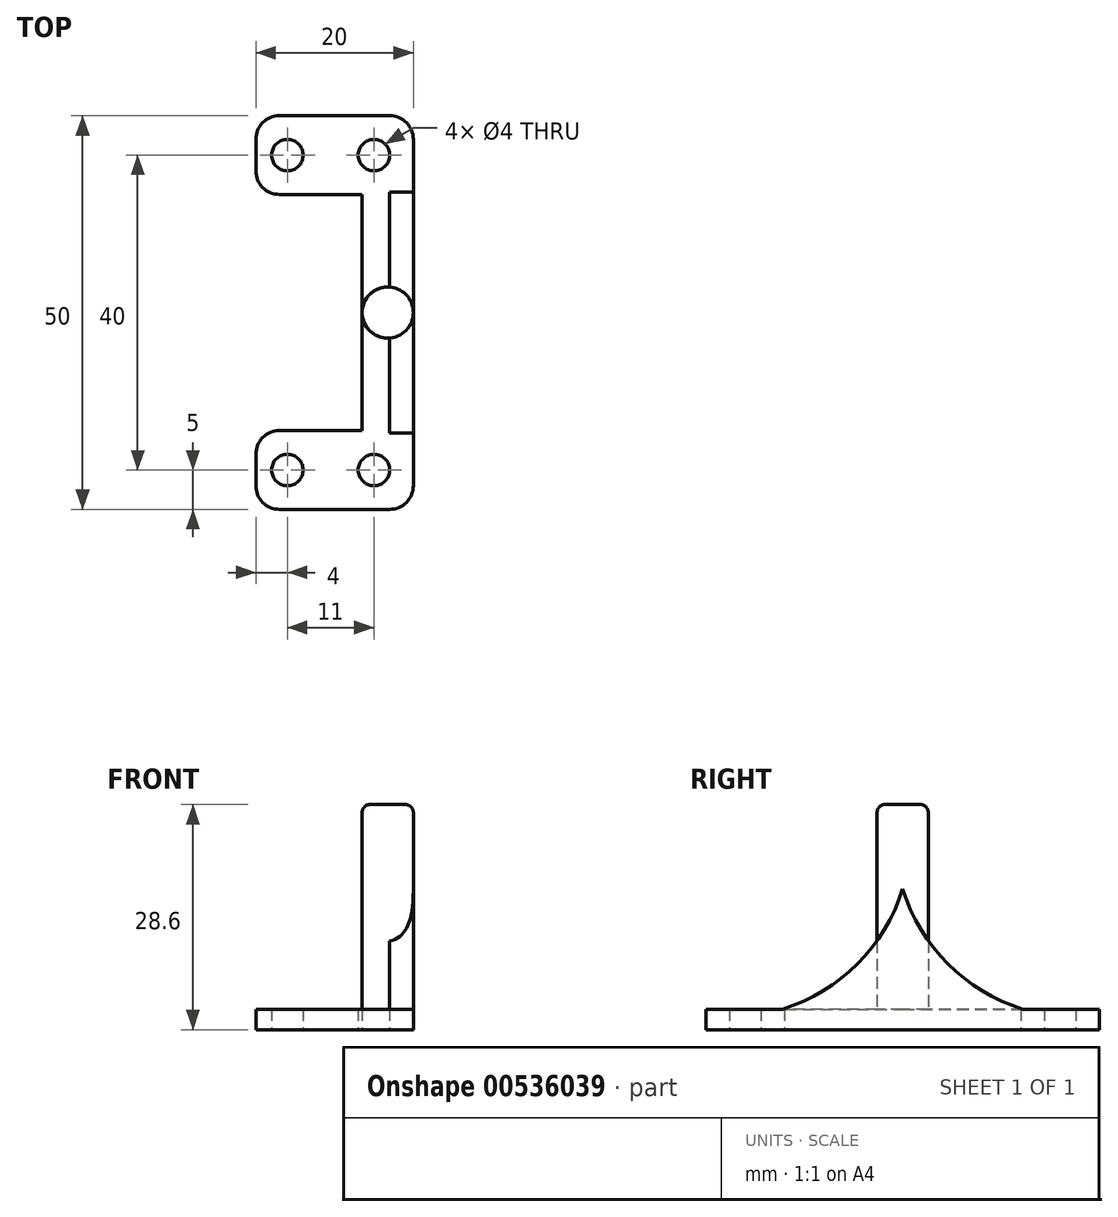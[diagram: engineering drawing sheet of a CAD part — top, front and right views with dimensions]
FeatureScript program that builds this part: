
annotation { "Feature Type Name" : "Feature", "Feature Type Description" : "" }
export const myFeature = defineFeature(function(context is Context, id is Id, definition is map)
    precondition{}
    {
        {
            var Q0;
            Q0=qCreatedBy(makeId("Top.planeOp"),FACE);
            var sketch = newSketch(context, id + "F0", { "sketchPlane" : qUnion([Q0])});
            skLineSegment(sketch, "E0.bottom", {"start": v(-20, 50) * mm, "end": v(0, 50) * mm});
            skLineSegment(sketch, "E0.right", {"start": v(0, 50) * mm, "end": v(0, 0) * mm});
            skLineSegment(sketch, "E1", {"start": v(-20, 50) * mm, "end": v(-20, 40) * mm});
            skLineSegment(sketch, "E2", {"start": v(-20, 10) * mm, "end": v(-6.5, 10) * mm});
            skLineSegment(sketch, "E3", {"start": v(-20, 40) * mm, "end": v(-6.5, 40) * mm});
            skCircle(sketch, "E4", {"center": v(-16, 45) * mm, "radius": 2 * mm});
            skCircle(sketch, "E5", {"center": v(-5, 45) * mm, "radius": 2 * mm});
            skCircle(sketch, "E6", {"center": v(-16, 5) * mm, "radius": 2 * mm});
            skCircle(sketch, "E7", {"center": v(-5, 5) * mm, "radius": 2 * mm});
            skLineSegment(sketch, "E8", {"start": v(-20, 10) * mm, "end": v(-20, 0) * mm});
            skLineSegment(sketch, "E9", {"start": v(-20, 0) * mm, "end": v(0, 0) * mm});
            skLineSegment(sketch, "E10", {"start": v(-6.5, 10) * mm, "end": v(-6.5, 40) * mm});
            skSolve(sketch);
        }
        {
            var Q0;
            Q0=makeQuery(id+"F0.imprint","IMPRINT",FACE,{"disambiguationData":[TD([[makeQuery(id+"F0.imprint","IMPRINT",EDGE,{"derivedFrom":sQuery(id+"F0.wireOp",EDGE,"E0.bottom")}),-1.0]])]});
            extrude(context, id + "F1", {"entities" : qUnion([Q0]), "depth" : 2.6 * mm, "offsetDistance" : 25 * mm});
        }
        {
            var Q0;
            Q0=makeQuery(id+"F1.opExtrude","CAP_FACE",FACE,{"disambiguationData":[OSD([sQuery(id+"F0.wireOp",EDGE,"E0.bottom"),sQuery(id+"F0.wireOp",EDGE,"E0.right"),sQuery(id+"F0.wireOp",EDGE,"E1"),sQuery(id+"F0.wireOp",EDGE,"5VIroKza-7dJa-2zdZ-CHlb-RgMu5IRMn0VJ"),sQuery(id+"F0.wireOp",EDGE,"E2"),sQuery(id+"F0.wireOp",EDGE,"E3"),sQuery(id+"F0.wireOp",EDGE,"E4"),sQuery(id+"F0.wireOp",EDGE,"E5"),sQuery(id+"F0.wireOp",EDGE,"E6"),sQuery(id+"F0.wireOp",EDGE,"E7"),sQuery(id+"F0.wireOp",EDGE,"E8"),sQuery(id+"F0.wireOp",EDGE,"E9"),sQuery(id+"F0.wireOp",EDGE,"IBOXaNeZ-d4qg-PSxC-ytc1-1ycewHry0LgP"),sQuery(id+"F0.wireOp",EDGE,"04bec0b6-6763-46f3-8f07-8cebe3ee9a99.trimOffspring")])],"isStart":false});
            var sketch = newSketch(context, id + "F2", { "sketchPlane" : qUnion([Q0])});
            skCircle(sketch, "E11", {"center": v(-3.25, 25) * mm, "radius": 3.25 * mm});
            skSolve(sketch);
        }
        {
            var Q0;
            Q0 = qSketchRegion(id + "F2", true);
            extrude(context, id + "F3", {"entities" : qUnion([Q0]), "operationType" : NewBodyOperationType.ADD, "depth" : 26 * mm, "offsetDistance" : 25 * mm});
        }
        {
            var Q0;
            Q0=makeQuery(id+"F1.opExtrude","SWEPT_EDGE",EDGE,{"disambiguationData":[OSD([sQuery(id+"F0.wireOp",EDGE,"E0.bottom"),sQuery(id+"F0.wireOp",EDGE,"E1")])]});
            var Q1;
            Q1=makeQuery(id+"F1.opExtrude","SWEPT_EDGE",EDGE,{"disambiguationData":[OSD([sQuery(id+"F0.wireOp",EDGE,"E1"),sQuery(id+"F0.wireOp",EDGE,"E3")])]});
            var Q2;
            Q2=makeQuery(id+"F1.opExtrude","SWEPT_EDGE",EDGE,{"disambiguationData":[OSD([sQuery(id+"F0.wireOp",EDGE,"E2"),sQuery(id+"F0.wireOp",EDGE,"E8")])]});
            var Q3;
            Q3=makeQuery(id+"F1.opExtrude","SWEPT_EDGE",EDGE,{"disambiguationData":[OSD([sQuery(id+"F0.wireOp",EDGE,"E8"),sQuery(id+"F0.wireOp",EDGE,"E9")])]});
            var Q4;
            Q4=makeQuery(id+"F1.opExtrude","SWEPT_EDGE",EDGE,{"disambiguationData":[OSD([sQuery(id+"F0.wireOp",EDGE,"E0.bottom"),sQuery(id+"F0.wireOp",EDGE,"E0.right")])]});
            var Q5;
            Q5=makeQuery(id+"F1.opExtrude","SWEPT_EDGE",EDGE,{"disambiguationData":[OSD([sQuery(id+"F0.wireOp",EDGE,"E0.right"),sQuery(id+"F0.wireOp",EDGE,"E9")])]});
            fillet(context, id + "F4", {"entities" : qUnion([Q0, Q1, Q2, Q3, Q4, Q5]), "radius" : 3 * mm, "tangentPropagation" : true, "allowEdgeOverflow" : false});
        }
        {
            var Q0;
            Q0=makeQuery(id+"F1.opExtrude","SWEPT_FACE",FACE,{"disambiguationData":[OSD([sQuery(id+"F0.wireOp",EDGE,"E0.right")])]});
            var sketch = newSketch(context, id + "F5", { "sketchPlane" : qUnion([Q0])});
            skArc(sketch, "E12", {"start": v(9.7, 2.6) * mm, "mid": v(19.26, 8.34) * mm, "end": v(25, 17.9) * mm});
            skArc(sketch, "E13", {"start": v(25, 17.9) * mm, "mid": v(30.74, 8.34) * mm, "end": v(40.3, 2.6) * mm});
            skSolve(sketch);
        }
        {
            var Q0;
            {var subQ0=sQuery(id+"F5.wireOp",EDGE,"E12");Q0=makeQuery(id+"F5.imprint","IMPRINT",FACE,{"disambiguationData":[TD([[makeQuery(id+"F5.imprint","IMPRINT",EDGE,{"derivedFrom":subQ0}),-1.0]])]});}
            extrude(context, id + "F6", {"entities" : qUnion([Q0]), "operationType" : NewBodyOperationType.ADD, "oppositeDirection" : true, "depth" : 3 * mm, "offsetDistance" : 25 * mm});
        }
        {
            var Q0;
            Q0=makeQuery(id+"F3.opExtrude","CAP_EDGE",EDGE,{"disambiguationData":[OSD([sQuery(id+"F2.wireOp",EDGE,"E11")])],"isStart":false});
            fillet(context, id + "F7", {"entities" : qUnion([Q0]), "radius" : 1 * mm, "tangentPropagation" : true, "allowEdgeOverflow" : false});
        }
    });
